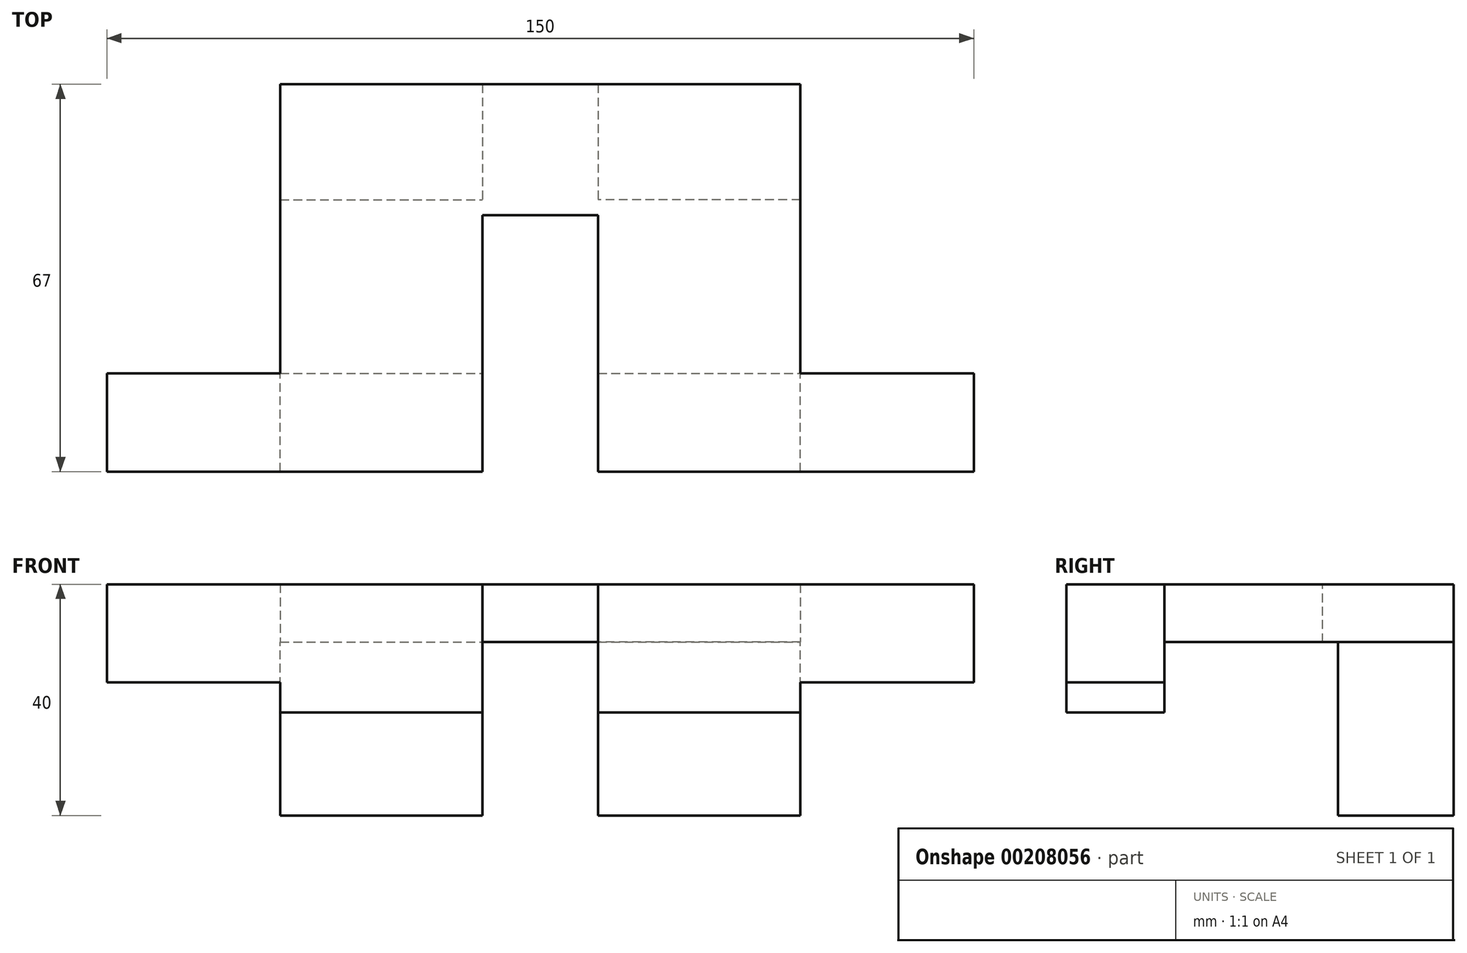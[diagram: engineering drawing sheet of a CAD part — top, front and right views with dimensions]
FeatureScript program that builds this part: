
annotation { "Feature Type Name" : "Feature", "Feature Type Description" : "" }
export const myFeature = defineFeature(function(context is Context, id is Id, definition is map)
    precondition{}
    {
        {
            var Q0;
            Q0=qCreatedBy(makeId("Top.planeOp"),FACE);
            var sketch = newSketch(context, id + "F5", { "sketchPlane" : qUnion([Q0])});
            skLineSegment(sketch, "E0.bottom", {"start": v(75, 8.5) * mm, "end": v(-75, 8.5) * mm});
            skLineSegment(sketch, "E0.top", {"start": v(75, -8.5) * mm, "end": v(-75, -8.5) * mm});
            skLineSegment(sketch, "E0.left", {"start": v(75, 8.5) * mm, "end": v(75, -8.5) * mm});
            skLineSegment(sketch, "E0.right", {"start": v(-75, 8.5) * mm, "end": v(-75, -8.5) * mm});
            skPoint(sketch, "E0.middle", {"position": v(0, 0) * mm});
            skSolve(sketch);
        }
        {
            var Q0;
            Q0 = qSketchRegion(id + "F5", true);
            extrude(context, id + "F6", {"entities" : qUnion([Q0]), "depth" : 17 * mm});
        }
        {
            var Q0;
            Q0=makeQuery(id+"F6.opExtrude","CAP_FACE",FACE,{"disambiguationData":[OSD([sQuery(id+"F5.wireOp",EDGE,"E0.bottom"),sQuery(id+"F5.wireOp",EDGE,"E0.top"),sQuery(id+"F5.wireOp",EDGE,"E0.left"),sQuery(id+"F5.wireOp",EDGE,"E0.right")])],"isStart":true});
            var sketch = newSketch(context, id + "F7", { "sketchPlane" : qUnion([Q0])});
            skLineSegment(sketch, "E1.bottom", {"start": v(45, 8.5) * mm, "end": v(-45, 8.5) * mm});
            skLineSegment(sketch, "E1.top", {"start": v(45, -8.5) * mm, "end": v(-45, -8.5) * mm});
            skLineSegment(sketch, "E1.left", {"start": v(45, 8.5) * mm, "end": v(45, -8.5) * mm});
            skLineSegment(sketch, "E1.right", {"start": v(-45, 8.5) * mm, "end": v(-45, -8.5) * mm});
            skSolve(sketch);
        }
        {
            var Q0;
            Q0 = qSketchRegion(id + "F7", true);
            extrude(context, id + "F8", {"entities" : qUnion([Q0]), "operationType" : NewBodyOperationType.ADD, "depth" : 5.16 * mm});
        }
        {
            var Q0;
            Q0=makeQuery(id+"F8.boolean.opBoolean","MERGE",FACE,{"derivedFrom":[makeQuery(id+"F6.opExtrude","SWEPT_FACE",FACE,{"disambiguationData":[OSD([sQuery(id+"F5.wireOp",EDGE,"E0.bottom")])]}),makeQuery(id+"F8.opExtrude","SWEPT_FACE",FACE,{"disambiguationData":[OSD([sQuery(id+"F7.wireOp",EDGE,"E1.top")])]})]});
            var sketch = newSketch(context, id + "F0", { "sketchPlane" : qUnion([Q0])});
            skLineSegment(sketch, "E2.bottom", {"start": v(-45, 17) * mm, "end": v(45, 17) * mm});
            skLineSegment(sketch, "E2.top", {"start": v(-45, 7) * mm, "end": v(45, 7) * mm});
            skLineSegment(sketch, "E2.left", {"start": v(-45, 17) * mm, "end": v(-45, 7) * mm});
            skLineSegment(sketch, "E2.right", {"start": v(45, 17) * mm, "end": v(45, 7) * mm});
            skSolve(sketch);
        }
        {
            var Q0;
            Q0 = qSketchRegion(id + "F0", true);
            extrude(context, id + "F9", {"entities" : qUnion([Q0]), "operationType" : NewBodyOperationType.ADD, "depth" : 50 * mm});
        }
        {
            var Q0;
            Q0=makeQuery(id+"F9.opExtrude","SWEPT_FACE",FACE,{"disambiguationData":[OSD([sQuery(id+"F0.wireOp",EDGE,"E2.top")])]});
            var sketch = newSketch(context, id + "F1", { "sketchPlane" : qUnion([Q0])});
            skLineSegment(sketch, "E3.bottom", {"start": v(-45, -58.5) * mm, "end": v(-10, -58.5) * mm});
            skLineSegment(sketch, "E3.top", {"start": v(-45, -38.5) * mm, "end": v(-10, -38.5) * mm});
            skLineSegment(sketch, "E3.left", {"start": v(-45, -58.5) * mm, "end": v(-45, -38.5) * mm});
            skLineSegment(sketch, "E3.right", {"start": v(-10, -58.5) * mm, "end": v(-10, -38.5) * mm});
            skSolve(sketch);
        }
        {
            var Q0;
            Q0 = qSketchRegion(id + "F1", true);
            extrude(context, id + "F10", {"entities" : qUnion([Q0]), "operationType" : NewBodyOperationType.ADD, "depth" : 30 * mm});
        }
        {
            var Q0;
            Q0=makeQuery(id+"F6.opExtrude","SWEPT_BODY",BODY,{"disambiguationData":[OSD([sQuery(id+"F5.wireOp",EDGE,"E0.bottom"),sQuery(id+"F5.wireOp",EDGE,"E0.top"),sQuery(id+"F5.wireOp",EDGE,"E0.left"),sQuery(id+"F5.wireOp",EDGE,"E0.right")])]});
            var Q1;
            Q1=qCreatedBy(makeId("Right.planeOp"),FACE);
            mirror(context, id + "F2", {"entities" : qUnion([Q0]), "mirrorPlane" : qUnion([Q1])});
        }
        {
            var Q0;
            Q0=makeQuery(id+"F2.opPattern","COPY",FACE,{"derivedFrom":makeQuery(id+"F9.boolean.opBoolean","MERGE",FACE,{"derivedFrom":[makeQuery(id+"F6.opExtrude","CAP_FACE",FACE,{"disambiguationData":[OSD([sQuery(id+"F5.wireOp",EDGE,"E0.bottom"),sQuery(id+"F5.wireOp",EDGE,"E0.top"),sQuery(id+"F5.wireOp",EDGE,"E0.left"),sQuery(id+"F5.wireOp",EDGE,"E0.right")])],"isStart":false}),makeQuery(id+"F9.opExtrude","SWEPT_FACE",FACE,{"disambiguationData":[OSD([sQuery(id+"F0.wireOp",EDGE,"E2.bottom")])]})]}),"instanceName":"1"});
            var sketch = newSketch(context, id + "F3", { "sketchPlane" : qUnion([Q0])});
            skSolve(sketch);
        }
        {
            var Q0;
            {var subQ5=sQuery(id+"F5.wireOp",EDGE,"E0.top");Q0=makeQuery(id+"F3.imprint","IMPRINT",FACE,{"disambiguationData":[TD([[makeQuery(id+"F3.imprint","IMPRINT",EDGE,{"derivedFrom":makeQuery(id+"F2.opPattern","COPY",EDGE,{"derivedFrom":makeQuery(id+"F6.opExtrude","CAP_EDGE",EDGE,{"disambiguationData":[OSD([subQ5])],"isStart":false}),"instanceName":"1"})}),1.0]])]});}
            var sketch = newSketch(context, id + "F4", { "sketchPlane" : qUnion([Q0])});
            skLineSegment(sketch, "E4.bottom", {"start": v(-10, 35.87) * mm, "end": v(10, 35.87) * mm});
            skLineSegment(sketch, "E4.top", {"start": v(-10, -8.5) * mm, "end": v(10, -8.5) * mm});
            skLineSegment(sketch, "E4.left", {"start": v(-10, 35.87) * mm, "end": v(-10, -8.5) * mm});
            skLineSegment(sketch, "E4.right", {"start": v(10, 35.87) * mm, "end": v(10, -8.5) * mm});
            skPoint(sketch, "E4.middle", {"position": v(0, 13.69) * mm});
            skSolve(sketch);
        }
        {
            var Q0;
            Q0 = qSketchRegion(id + "F4", true);
            extrude(context, id + "F11", {"entities" : qUnion([Q0]), "operationType" : NewBodyOperationType.REMOVE, "oppositeDirection" : true, "depth" : 50 * mm});
        }
    });
